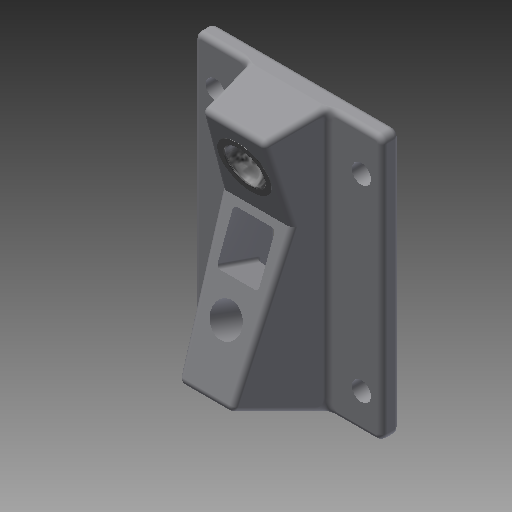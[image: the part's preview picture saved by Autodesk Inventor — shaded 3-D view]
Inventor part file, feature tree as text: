
AUTODESK INVENTOR PART (.ipt)
format: ipt  version: 2019 (Build 230136000, 136)  size: 588,288 bytes
history: native  units: mm
features: sketch x7, extrude x6, other x4, fillet x3, loft x2, hole x1, revolve x1
ambient origin geometry x8: Origin, YZ Plane, XZ Plane, XY Plane, X Axis, Y Axis, Z Axis, Center Point
bodies: Solido1 (feature_tree)
feature tree (24):
  extrude  "Estrusione1"  Depth=76.0mm
  extrude  "Estrusione2"  Depth=54.0mm
  extrude  "Estrusione3"  Depth=2.0mm
  extrude  "Estrusione4"  Depth=5.0mm TaperAngle=0.0deg
  fillet  "Raccordo1"  Radius=23.0mm
  sketch  "Schizzo5"
  loft  "Loft1"
  sketch  "Schizzo10"
  other  "Piano di lavoro1"
  loft  "Loft2"
  hole  "Foro1"  [1 undecoded]
  fillet  "Raccordo2"  Radius=10.0mm
  revolve  "Rivoluzione1"
  extrude  "Estrusione5"  Depth=24.0mm TaperAngle=0.0deg
  fillet  "Raccordo3"  Radius=15.0mm
  extrude  "Estrusione6"  Depth=46.0mm
  sketch  "Schizzo3"
  other  "Linea chiusa proiettata1"
  sketch  "Schizzo4"
  other  "Linea chiusa proiettata2"
  sketch  "Schizzo12"
  other  "Linea chiusa proiettata4"
  sketch  "Schizzo13"
  sketch  "Schizzo15"
note: 1 required parameter value undecoded (feature->parameter linkage not recoverable at this tier; creation-order binding heuristic only, values carry confidence <= 0.55)
